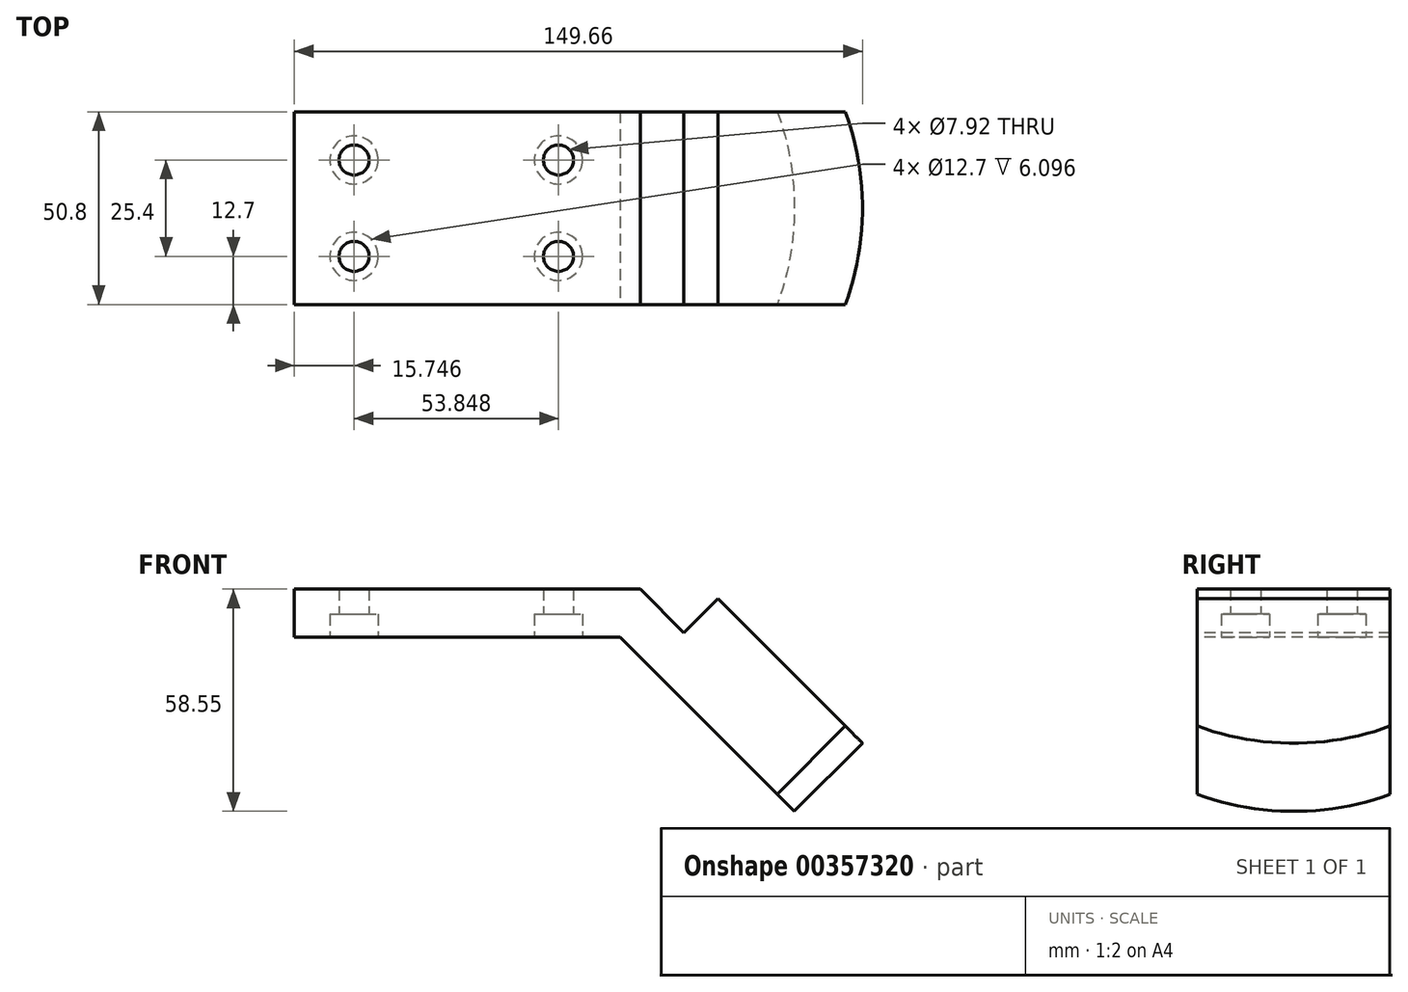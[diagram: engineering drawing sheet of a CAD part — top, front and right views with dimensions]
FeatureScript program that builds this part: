
annotation { "Feature Type Name" : "Feature", "Feature Type Description" : "" }
export const myFeature = defineFeature(function(context is Context, id is Id, definition is map)
    precondition{}
    {
        {
            var Q0;
            Q0=qCreatedBy(makeId("Front.planeOp"),FACE);
            var sketch = newSketch(context, id + "F0", { "sketchPlane" : qUnion([Q0])});
            skLineSegment(sketch, "E0", {"start": v(-17.57, 2.51) * mm, "end": v(-17.57, -10.19) * mm});
            skLineSegment(sketch, "E1", {"start": v(-17.57, -10.19) * mm, "end": v(68.28, -10.19) * mm});
            skLineSegment(sketch, "E2", {"start": v(68.28, -10.19) * mm, "end": v(114.13, -56.04) * mm});
            skLineSegment(sketch, "E3", {"start": v(114.13, -56.04) * mm, "end": v(132.1, -38.08) * mm});
            skLineSegment(sketch, "E4", {"start": v(132.1, -38.08) * mm, "end": v(94.02, 0) * mm});
            skLineSegment(sketch, "E5", {"start": v(94.02, 0) * mm, "end": v(85.04, -8.98) * mm});
            skLineSegment(sketch, "E6", {"start": v(85.04, -8.98) * mm, "end": v(73.54, 2.51) * mm});
            skLineSegment(sketch, "E7", {"start": v(73.54, 2.51) * mm, "end": v(-17.57, 2.51) * mm});
            skSolve(sketch);
        }
        {
            var Q0;
            Q0=qSketchRegion(id+"F0",true);
            extrude(context, id + "F1", {"entities" : qUnion([Q0]), "oppositeDirection" : true, "depth" : 50.8 * mm});
        }
        {
            var Q0;
            Q0=makeQuery(id+"F1.opExtrude","SWEPT_FACE",FACE,{"disambiguationData":[OSD([sQuery(id+"F0.wireOp",EDGE,"E1")])]});
            cPlane(context, id + "F2", {"entities" : qUnion([Q0]), "cplaneType" : CPlaneType.OFFSET, "offset" : 0 * mm, "width" : 152.4 * mm, "height" : 152.4 * mm});
        }
        {
            var Q0;
            Q0=qCreatedBy(id+"F2.planeOp",FACE);
            var sketch = newSketch(context, id + "F3", { "sketchPlane" : qUnion([Q0])});
            skCircle(sketch, "E8", {"center": v(-1.82, -12.7) * mm, "radius": 3.96 * mm});
            skCircle(sketch, "E9", {"center": v(-1.82, -38.1) * mm, "radius": 3.96 * mm});
            skCircle(sketch, "E10", {"center": v(52.02, -12.7) * mm, "radius": 3.96 * mm});
            skCircle(sketch, "E11", {"center": v(52.02, -38.1) * mm, "radius": 3.96 * mm});
            skSolve(sketch);
        }
        {
            var Q0;
            Q0=sQuery(id+"F3.wireOp",VERTEX,"E8.center");
            var Q1;
            Q1=sQuery(id+"F3.wireOp",VERTEX,"E9.center");
            var Q2;
            Q2=sQuery(id+"F3.wireOp",VERTEX,"E10.center");
            var Q3;
            Q3=sQuery(id+"F3.wireOp",VERTEX,"E11.center");
            var Q4;
            Q4=makeQuery(id+"F1.opExtrude","SWEPT_BODY",BODY,{"disambiguationData":[OSD([sQuery(id+"F0.wireOp",EDGE,"E0"),sQuery(id+"F0.wireOp",EDGE,"E1"),sQuery(id+"F0.wireOp",EDGE,"E2"),sQuery(id+"F0.wireOp",EDGE,"E3"),sQuery(id+"F0.wireOp",EDGE,"E4"),sQuery(id+"F0.wireOp",EDGE,"E5"),sQuery(id+"F0.wireOp",EDGE,"E6"),sQuery(id+"F0.wireOp",EDGE,"E7")])]});
            hole(context, id + "F4", {"style" : HoleStyle.C_BORE, "endStyle" : HoleEndStyle.THROUGH, "holeDiameter" : 7.92 * mm, "cBoreDiameter" : 12.7 * mm, "cBoreDepth" : 6.1 * mm, "isTappedThrough" : true, "tappedDepth" : 12.7 * mm, "tapClearance" : 3, "startFromSketch" : true, "locations" : qUnion([Q0, Q1, Q2, Q3]), "scope" : qUnion([Q4])});
        }
        {
            var Q0;
            Q0=makeQuery(id+"F1.opExtrude","SWEPT_FACE",FACE,{"disambiguationData":[OSD([sQuery(id+"F0.wireOp",EDGE,"E4")])]});
            cPlane(context, id + "F5", {"entities" : qUnion([Q0]), "cplaneType" : CPlaneType.OFFSET, "offset" : 0 * mm, "width" : 152.4 * mm, "height" : 152.4 * mm});
        }
        {
            var Q0;
            Q0=makeQuery(id+"F1.opExtrude","SWEPT_FACE",FACE,{"disambiguationData":[OSD([sQuery(id+"F0.wireOp",EDGE,"E3")])]});
            cPlane(context, id + "F6", {"entities" : qUnion([Q0]), "cplaneType" : CPlaneType.OFFSET, "offset" : 0 * mm, "width" : 152.4 * mm, "height" : 152.4 * mm});
        }
        {
            var Q0;
            Q0=qCreatedBy(id+"F5.planeOp",FACE);
            var sketch = newSketch(context, id + "F7", { "sketchPlane" : qUnion([Q0])});
            skArc(sketch, "E12", {"start": v(0, -113.96) * mm, "mid": v(25.4, -120.33) * mm, "end": v(50.8, -113.96) * mm});
            skLineSegment(sketch, "E13", {"start": v(0, -113.96) * mm, "end": v(0, -123.43) * mm});
            skLineSegment(sketch, "E14", {"start": v(0, -123.43) * mm, "end": v(50.8, -123.43) * mm});
            skLineSegment(sketch, "E15", {"start": v(50.8, -123.43) * mm, "end": v(50.8, -113.96) * mm});
            skSolve(sketch);
        }
        {
            var Q0;
            Q0=qSketchRegion(id+"F7",true);
            extrude(context, id + "F8", {"entities" : qUnion([Q0]), "operationType" : NewBodyOperationType.REMOVE, "endBound" : BoundingType.THROUGH_ALL, "oppositeDirection" : true, "depth" : 25.4 * mm});
        }
        {
            var Q0;
            Q0=qCreatedBy(id+"F6.planeOp",FACE);
            var sketch = newSketch(context, id + "F9", { "sketchPlane" : qUnion([Q0])});
            skLineSegment(sketch, "E16", {"start": v(66.48, -15.75) * mm, "end": v(60.38, -15.75) * mm});
            skLineSegment(sketch, "E17", {"start": v(60.38, -15.75) * mm, "end": v(60.38, -9.65) * mm});
            skLineSegment(sketch, "E18", {"start": v(60.38, -9.65) * mm, "end": v(53.78, -9.65) * mm});
            skLineSegment(sketch, "E19", {"start": v(53.78, -9.65) * mm, "end": v(53.78, -41.15) * mm});
            skLineSegment(sketch, "E20", {"start": v(53.78, -41.15) * mm, "end": v(60.38, -41.15) * mm});
            skLineSegment(sketch, "E21", {"start": v(60.38, -41.15) * mm, "end": v(60.38, -35.05) * mm});
            skLineSegment(sketch, "E22", {"start": v(60.38, -35.05) * mm, "end": v(66.48, -35.05) * mm});
            skLineSegment(sketch, "E23", {"start": v(66.48, -35.05) * mm, "end": v(66.48, -15.75) * mm});
            skSolve(sketch);
        }
        {
            var Q0;
            Q0=qSketchRegion(id+"F9",true);
            extrude(context, id + "F10", {"entities" : qUnion([Q0]), "operationType" : NewBodyOperationType.REMOVE, "endBound" : BoundingType.THROUGH_ALL, "oppositeDirection" : true, "depth" : 25.4 * mm});
        }
    });
